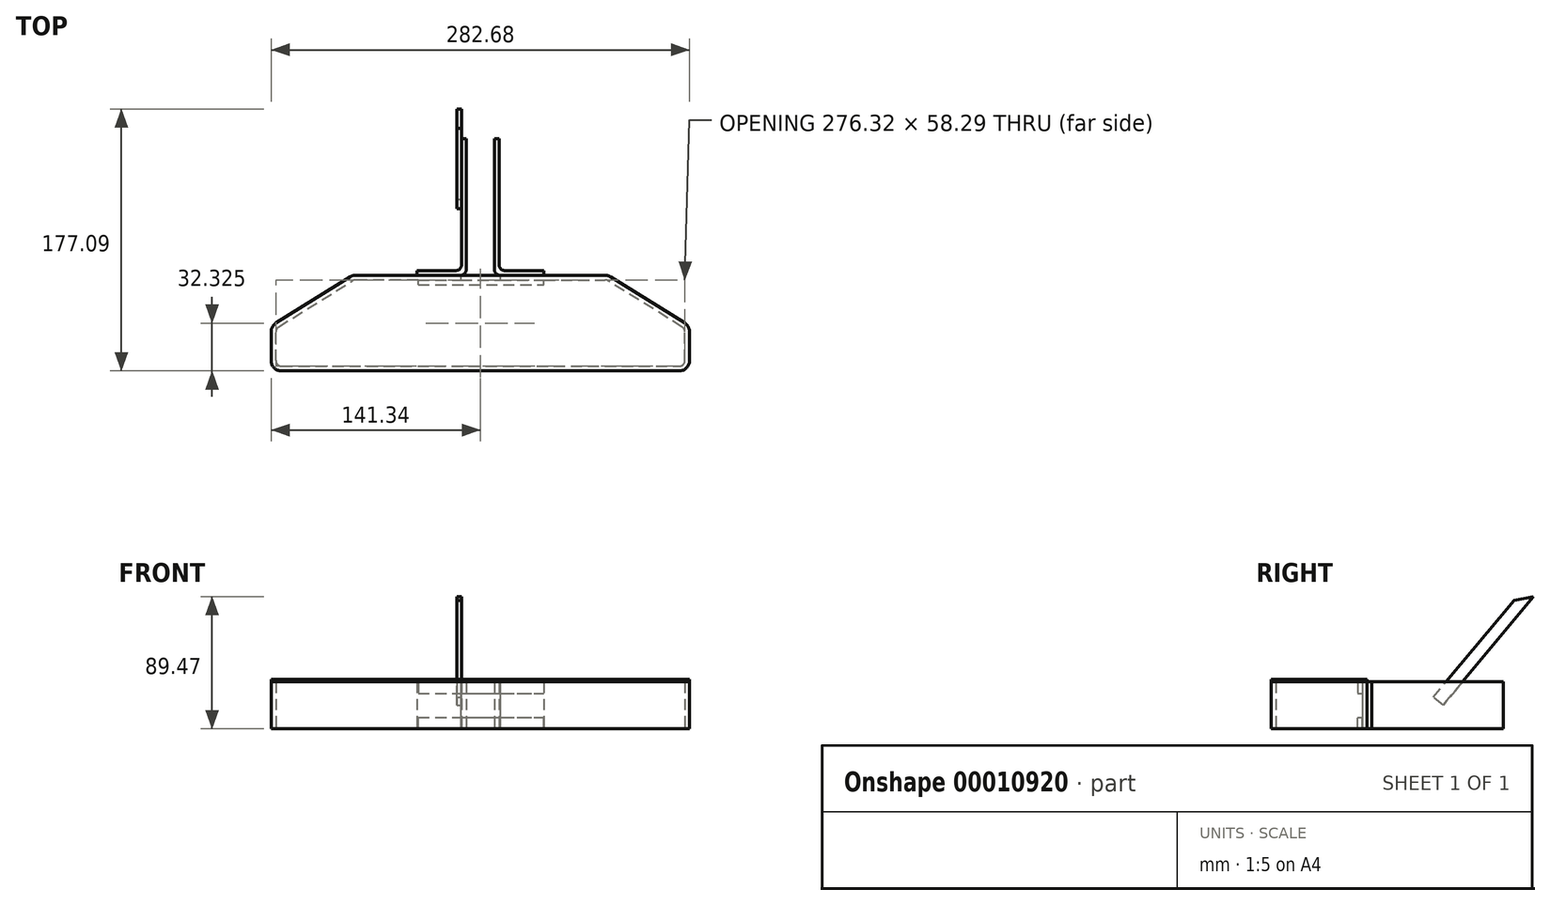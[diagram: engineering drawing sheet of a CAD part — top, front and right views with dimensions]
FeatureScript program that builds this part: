
annotation { "Feature Type Name" : "Feature", "Feature Type Description" : "" }
export const myFeature = defineFeature(function(context is Context, id is Id, definition is map)
    precondition{}
    {
        {
            var Q0;
            Q0=qCreatedBy(makeId("Top.planeOp"),FACE);
            var sketch = newSketch(context, id + "F0", { "sketchPlane" : qUnion([Q0])});
            skLineSegment(sketch, "E0", {"start": v(98.84, -71.17) * mm, "end": v(98.84, -68) * mm});
            skLineSegment(sketch, "E1.0.MirrorCS", {"start": v(89.32, 85.68) * mm, "end": v(86.14, 85.68) * mm});
            skLineSegment(sketch, "E1.2.MirrorCS", {"start": v(86.14, 0.46) * mm, "end": v(86.14, 85.68) * mm});
            skLineSegment(sketch, "E1.6.MirrorCS", {"start": v(89.32, 47.12) * mm, "end": v(89.32, 85.68) * mm});
            skLineSegment(sketch, "E1.7.MirrorCS", {"start": v(-37.52, -41.47) * mm, "end": v(12.52, -10.28) * mm});
            skLineSegment(sketch, "E1.8.MirrorCS", {"start": v(98.84, -68) * mm, "end": v(-35.5, -68) * mm});
            skLineSegment(sketch, "E1.9.MirrorCS", {"start": v(89.32, -2.71) * mm, "end": v(89.32, 47.12) * mm});
            skLineSegment(sketch, "E1.14.MirrorCS", {"start": v(-39.32, -64.18) * mm, "end": v(-39.32, -44.7) * mm});
            skLineSegment(sketch, "E2.0", {"start": v(55.97, -3.35) * mm, "end": v(82.33, -3.35) * mm});
            skLineSegment(sketch, "E3", {"start": v(55.97, -3.35) * mm, "end": v(55.97, -6.52) * mm});
            skPoint(sketch, "E4.visualSharp", {"position": v(86.14, -3.35) * mm});
            skArc(sketch, "E4.filletArc", {"start": v(82.33, -3.35) * mm, "mid": v(85.02, -2.23) * mm, "end": v(86.14, 0.46) * mm});
            skLineSegment(sketch, "E5", {"start": v(55.97, -6.52) * mm, "end": v(85.5, -6.52) * mm});
            skArc(sketch, "E6.filletArc", {"start": v(85.5, -6.52) * mm, "mid": v(88.2, -5.4) * mm, "end": v(89.32, -2.71) * mm});
            skLineSegment(sketch, "E7", {"start": v(85.5, -9.7) * mm, "end": v(14.54, -9.7) * mm});
            skLineSegment(sketch, "E8", {"start": v(85.5, -6.52) * mm, "end": v(85.5, -9.7) * mm});
            skPoint(sketch, "E1.13.MirrorCS.end.orphan", {"position": v(-42.5, -39.42) * mm});
            skPoint(sketch, "E1.1.MirrorCS.start.orphan", {"position": v(10.07, -6.52) * mm});
            skPoint(sketch, "E9.visualSharp", {"position": v(-39.32, -42.6) * mm});
            skArc(sketch, "E9.filletArc", {"start": v(-37.52, -41.47) * mm, "mid": v(-38.84, -42.86) * mm, "end": v(-39.32, -44.7) * mm});
            skPoint(sketch, "E10.visualSharp", {"position": v(-39.32, -68) * mm});
            skArc(sketch, "E10.filletArc", {"start": v(-39.32, -64.18) * mm, "mid": v(-38.2, -66.88) * mm, "end": v(-35.5, -68) * mm});
            skPoint(sketch, "E11.visualSharp", {"position": v(13.45, -9.7) * mm});
            skArc(sketch, "E11.filletArc", {"start": v(14.54, -9.7) * mm, "mid": v(13.49, -9.85) * mm, "end": v(12.52, -10.28) * mm});
            skLineSegment(sketch, "E12.0", {"start": v(98.84, -71.17) * mm, "end": v(-35.5, -71.17) * mm});
            skArc(sketch, "E12.1", {"start": v(-42.5, -64.18) * mm, "mid": v(-40.45, -69.12) * mm, "end": v(-35.5, -71.17) * mm});
            skLineSegment(sketch, "E12.2", {"start": v(-42.5, -64.18) * mm, "end": v(-42.5, -44.7) * mm});
            skArc(sketch, "E12.3", {"start": v(-39.2, -38.77) * mm, "mid": v(-41.62, -41.31) * mm, "end": v(-42.5, -44.7) * mm});
            skLineSegment(sketch, "E12.4", {"start": v(-39.2, -38.77) * mm, "end": v(10.84, -7.58) * mm});
            skArc(sketch, "E12.5", {"start": v(14.54, -6.52) * mm, "mid": v(12.61, -6.79) * mm, "end": v(10.84, -7.58) * mm});
            skLineSegment(sketch, "E12.6", {"start": v(85.5, -6.52) * mm, "end": v(14.54, -6.52) * mm});
            skArc(sketch, "E13.0.MirrorCS", {"start": v(112.18, -6.52) * mm, "mid": v(109.48, -5.4) * mm, "end": v(108.37, -2.71) * mm});
            skArc(sketch, "E13.1.MirrorCS", {"start": v(183.14, -9.7) * mm, "mid": v(184.2, -9.85) * mm, "end": v(185.16, -10.28) * mm});
            skArc(sketch, "E13.2.MirrorCS", {"start": v(183.14, -6.52) * mm, "mid": v(185.07, -6.79) * mm, "end": v(186.84, -7.58) * mm});
            skArc(sketch, "E13.3.MirrorCS", {"start": v(236.89, -38.77) * mm, "mid": v(239.3, -41.31) * mm, "end": v(240.18, -44.7) * mm});
            skArc(sketch, "E13.4.MirrorCS", {"start": v(115.35, -3.35) * mm, "mid": v(112.66, -2.23) * mm, "end": v(111.54, 0.46) * mm});
            skArc(sketch, "E13.5.MirrorCS", {"start": v(235.2, -41.47) * mm, "mid": v(236.52, -42.86) * mm, "end": v(237, -44.7) * mm});
            skLineSegment(sketch, "E13.6.MirrorCS", {"start": v(108.37, 85.68) * mm, "end": v(111.54, 85.68) * mm});
            skLineSegment(sketch, "E13.7.MirrorCS", {"start": v(112.18, -6.52) * mm, "end": v(112.18, -9.7) * mm});
            skLineSegment(sketch, "E13.8.MirrorCS", {"start": v(141.71, -3.35) * mm, "end": v(141.71, -6.52) * mm});
            skArc(sketch, "E13.9.MirrorCS", {"start": v(237, -64.18) * mm, "mid": v(235.88, -66.88) * mm, "end": v(233.19, -68) * mm});
            skLineSegment(sketch, "E13.10.MirrorCS", {"start": v(108.37, 47.12) * mm, "end": v(108.37, 85.68) * mm});
            skLineSegment(sketch, "E13.11.MirrorCS", {"start": v(108.37, -2.71) * mm, "end": v(108.37, 47.12) * mm});
            skLineSegment(sketch, "E13.13.MirrorCS", {"start": v(112.18, -9.7) * mm, "end": v(183.14, -9.7) * mm});
            skLineSegment(sketch, "E13.14.MirrorCS", {"start": v(111.54, 0.46) * mm, "end": v(111.54, 85.68) * mm});
            skPoint(sketch, "E13.15.MirrorP", {"position": v(184.23, -9.7) * mm});
            skArc(sketch, "E13.16.MirrorCS", {"start": v(240.18, -64.18) * mm, "mid": v(238.13, -69.12) * mm, "end": v(233.19, -71.17) * mm});
            skLineSegment(sketch, "E13.17.MirrorCS", {"start": v(235.2, -41.47) * mm, "end": v(185.16, -10.28) * mm});
            skLineSegment(sketch, "E13.18.MirrorCS", {"start": v(240.18, -64.18) * mm, "end": v(240.18, -44.7) * mm});
            skPoint(sketch, "E13.19.MirrorP", {"position": v(240.17, -39.42) * mm});
            skLineSegment(sketch, "E13.20.MirrorCS", {"start": v(141.71, -6.52) * mm, "end": v(112.18, -6.52) * mm});
            skPoint(sketch, "E13.21.MirrorP", {"position": v(237, -42.6) * mm});
            skPoint(sketch, "E13.22.MirrorP", {"position": v(187.61, -6.52) * mm});
            skPoint(sketch, "E13.23.MirrorP", {"position": v(111.54, -3.35) * mm});
            skLineSegment(sketch, "E13.24.MirrorCS", {"start": v(141.71, -3.35) * mm, "end": v(115.35, -3.35) * mm});
            skLineSegment(sketch, "E13.25.MirrorCS", {"start": v(236.89, -38.77) * mm, "end": v(186.84, -7.58) * mm});
            skLineSegment(sketch, "E13.26.MirrorCS", {"start": v(237, -64.18) * mm, "end": v(237, -44.7) * mm});
            skLineSegment(sketch, "E13.27.MirrorCS", {"start": v(112.18, -6.52) * mm, "end": v(183.14, -6.52) * mm});
            skPoint(sketch, "E13.28.MirrorP", {"position": v(237, -68) * mm});
            skLineSegment(sketch, "E14.0.MirrorCS", {"start": v(98.84, -71.17) * mm, "end": v(233.19, -71.17) * mm});
            skLineSegment(sketch, "E15.0.MirrorCS", {"start": v(98.84, -68) * mm, "end": v(233.19, -68) * mm});
            skSolve(sketch);
        }
        {
            var Q0;
            Q0 = qSketchRegion(id + "F0", true);
            extrude(context, id + "F1", {"entities" : qUnion([Q0]), "depth" : 31.75 * mm});
        }
        {
            var Q0;
            Q0=makeQuery(id+"F1.opExtrude","SWEPT_FACE",FACE,{"disambiguationData":[OSD([sQuery(id+"F0.wireOp",EDGE,"E7")])]});
            var sketch = newSketch(context, id + "F2", { "sketchPlane" : qUnion([Q0])});
            skLineSegment(sketch, "E16.bottom", {"start": v(56.85, 31.75) * mm, "end": v(141.88, 31.75) * mm});
            skLineSegment(sketch, "E16.top", {"start": v(56.85, 23.9) * mm, "end": v(141.88, 23.9) * mm});
            skLineSegment(sketch, "E16.left", {"start": v(56.85, 31.75) * mm, "end": v(56.85, 23.9) * mm});
            skLineSegment(sketch, "E16.right", {"start": v(141.88, 31.75) * mm, "end": v(141.88, 23.9) * mm});
            skLineSegment(sketch, "E17.0.MirrorCS", {"start": v(56.85, 0) * mm, "end": v(141.88, 0) * mm});
            skLineSegment(sketch, "E17.1.MirrorCS", {"start": v(56.85, 7.86) * mm, "end": v(141.88, 7.86) * mm});
            skLineSegment(sketch, "E17.2.MirrorCS", {"start": v(56.85, 0) * mm, "end": v(56.85, 7.86) * mm});
            skLineSegment(sketch, "E17.3.MirrorCS", {"start": v(141.88, 0) * mm, "end": v(141.88, 7.86) * mm});
            skPoint(sketch, "E18.start.orphan", {"position": v(85.5, 15.88) * mm});
            skSolve(sketch);
        }
        {
            var Q0;
            Q0 = qSketchRegion(id + "F2", true);
            extrude(context, id + "F3", {"entities" : qUnion([Q0]), "operationType" : NewBodyOperationType.ADD, "depth" : 3.17 * mm});
        }
        {
            var Q0;
            Q0=makeQuery(id+"F3.boolean.opBoolean","MERGE",FACE,{"derivedFrom":[makeQuery(id+"F1.opExtrude","CAP_FACE",FACE,{"disambiguationData":[OSD([sQuery(id+"F0.wireOp",EDGE,"E1.0.MirrorCS"),sQuery(id+"F0.wireOp",EDGE,"E1.2.MirrorCS"),sQuery(id+"F0.wireOp",EDGE,"E1.6.MirrorCS"),sQuery(id+"F0.wireOp",EDGE,"E1.7.MirrorCS"),sQuery(id+"F0.wireOp",EDGE,"E1.8.MirrorCS"),sQuery(id+"F0.wireOp",EDGE,"E1.9.MirrorCS"),sQuery(id+"F0.wireOp",EDGE,"E1.14.MirrorCS"),sQuery(id+"F0.wireOp",EDGE,"E2.0"),sQuery(id+"F0.wireOp",EDGE,"E3"),sQuery(id+"F0.wireOp",EDGE,"E4.filletArc"),sQuery(id+"F0.wireOp",EDGE,"E6.filletArc"),sQuery(id+"F0.wireOp",EDGE,"E7"),sQuery(id+"F0.wireOp",EDGE,"E8"),sQuery(id+"F0.wireOp",EDGE,"E9.filletArc"),sQuery(id+"F0.wireOp",EDGE,"E10.filletArc"),sQuery(id+"F0.wireOp",EDGE,"E11.filletArc"),sQuery(id+"F0.wireOp",EDGE,"E12.0"),sQuery(id+"F0.wireOp",EDGE,"E12.1"),sQuery(id+"F0.wireOp",EDGE,"E12.2"),sQuery(id+"F0.wireOp",EDGE,"E12.3"),sQuery(id+"F0.wireOp",EDGE,"E12.4"),sQuery(id+"F0.wireOp",EDGE,"E12.5"),sQuery(id+"F0.wireOp",EDGE,"E12.6"),sQuery(id+"F0.wireOp",EDGE,"E13.0.MirrorCS"),sQuery(id+"F0.wireOp",EDGE,"E13.1.MirrorCS"),sQuery(id+"F0.wireOp",EDGE,"E13.2.MirrorCS"),sQuery(id+"F0.wireOp",EDGE,"E13.3.MirrorCS"),sQuery(id+"F0.wireOp",EDGE,"E13.4.MirrorCS"),sQuery(id+"F0.wireOp",EDGE,"E13.5.MirrorCS"),sQuery(id+"F0.wireOp",EDGE,"E13.6.MirrorCS"),sQuery(id+"F0.wireOp",EDGE,"E13.7.MirrorCS"),sQuery(id+"F0.wireOp",EDGE,"E13.8.MirrorCS"),sQuery(id+"F0.wireOp",EDGE,"E13.9.MirrorCS"),sQuery(id+"F0.wireOp",EDGE,"E13.10.MirrorCS"),sQuery(id+"F0.wireOp",EDGE,"E13.11.MirrorCS"),sQuery(id+"F0.wireOp",EDGE,"E13.13.MirrorCS"),sQuery(id+"F0.wireOp",EDGE,"E13.14.MirrorCS"),sQuery(id+"F0.wireOp",EDGE,"E13.16.MirrorCS"),sQuery(id+"F0.wireOp",EDGE,"E13.17.MirrorCS"),sQuery(id+"F0.wireOp",EDGE,"E13.18.MirrorCS"),sQuery(id+"F0.wireOp",EDGE,"E13.24.MirrorCS"),sQuery(id+"F0.wireOp",EDGE,"E13.25.MirrorCS"),sQuery(id+"F0.wireOp",EDGE,"E13.26.MirrorCS"),sQuery(id+"F0.wireOp",EDGE,"E13.27.MirrorCS"),sQuery(id+"F0.wireOp",EDGE,"E14.0.MirrorCS"),sQuery(id+"F0.wireOp",EDGE,"E15.0.MirrorCS")])],"isStart":false}),makeQuery(id+"F3.opExtrude","SWEPT_FACE",FACE,{"disambiguationData":[OSD([sQuery(id+"F2.wireOp",EDGE,"E16.bottom")])]})]});
            var sketch = newSketch(context, id + "F4", { "sketchPlane" : qUnion([Q0])});
            skLineSegment(sketch, "E19.0", {"start": v(141.71, -6.52) * mm, "end": v(183.14, -6.52) * mm});
            skArc(sketch, "E19.1", {"start": v(183.14, -6.52) * mm, "mid": v(185.07, -6.79) * mm, "end": v(186.84, -7.58) * mm});
            skLineSegment(sketch, "E19.2", {"start": v(236.89, -38.77) * mm, "end": v(186.84, -7.58) * mm});
            skArc(sketch, "E19.3", {"start": v(236.89, -38.77) * mm, "mid": v(239.3, -41.31) * mm, "end": v(240.18, -44.7) * mm});
            skLineSegment(sketch, "E19.4", {"start": v(240.18, -64.18) * mm, "end": v(240.18, -44.7) * mm});
            skArc(sketch, "E19.5", {"start": v(240.18, -64.18) * mm, "mid": v(238.13, -69.12) * mm, "end": v(233.19, -71.17) * mm});
            skLineSegment(sketch, "E19.6", {"start": v(233.19, -71.17) * mm, "end": v(-35.5, -71.17) * mm});
            skArc(sketch, "E19.7", {"start": v(-42.5, -64.18) * mm, "mid": v(-40.45, -69.12) * mm, "end": v(-35.5, -71.17) * mm});
            skLineSegment(sketch, "E19.8", {"start": v(-42.5, -64.18) * mm, "end": v(-42.5, -44.7) * mm});
            skArc(sketch, "E19.9", {"start": v(-39.2, -38.77) * mm, "mid": v(-41.62, -41.31) * mm, "end": v(-42.5, -44.7) * mm});
            skLineSegment(sketch, "E19.10", {"start": v(-39.2, -38.77) * mm, "end": v(10.84, -7.58) * mm});
            skArc(sketch, "E19.11", {"start": v(14.54, -6.52) * mm, "mid": v(12.61, -6.79) * mm, "end": v(10.84, -7.58) * mm});
            skLineSegment(sketch, "E19.12", {"start": v(55.97, -6.52) * mm, "end": v(14.54, -6.52) * mm});
            skLineSegment(sketch, "E20", {"start": v(55.97, -6.52) * mm, "end": v(141.71, -6.52) * mm});
            skSolve(sketch);
        }
        {
            var Q0;
            Q0 = qSketchRegion(id + "F4", true);
            extrude(context, id + "F5", {"entities" : qUnion([Q0]), "depth" : 1.59 * mm});
        }
        {
            var Q0;
            Q0=makeQuery(id+"F1.opExtrude","SWEPT_FACE",FACE,{"disambiguationData":[OSD([sQuery(id+"F0.wireOp",EDGE,"E1.2.MirrorCS")])]});
            var sketch = newSketch(context, id + "F6", { "sketchPlane" : qUnion([Q0])});
            skLineSegment(sketch, "E21", {"start": v(-38.34, 31.98) * mm, "end": v(-38.34, 90.4) * mm});
            skLineSegment(sketch, "E22", {"start": v(-38.34, 21.48) * mm, "end": v(-92.82, 86.92) * mm});
            skLineSegment(sketch, "E23", {"start": v(-105.92, 89.47) * mm, "end": v(-44.83, 16.08) * mm});
            skLineSegment(sketch, "E24", {"start": v(-44.83, 16.08) * mm, "end": v(-38.34, 21.48) * mm});
            skLineSegment(sketch, "E25", {"start": v(-105.92, 89.47) * mm, "end": v(-92.82, 86.92) * mm});
            skSolve(sketch);
        }
        {
            var Q0;
            Q0 = qSketchRegion(id + "F6", true);
            extrude(context, id + "F7", {"entities" : qUnion([Q0]), "depth" : 3.17 * mm});
        }
    });
